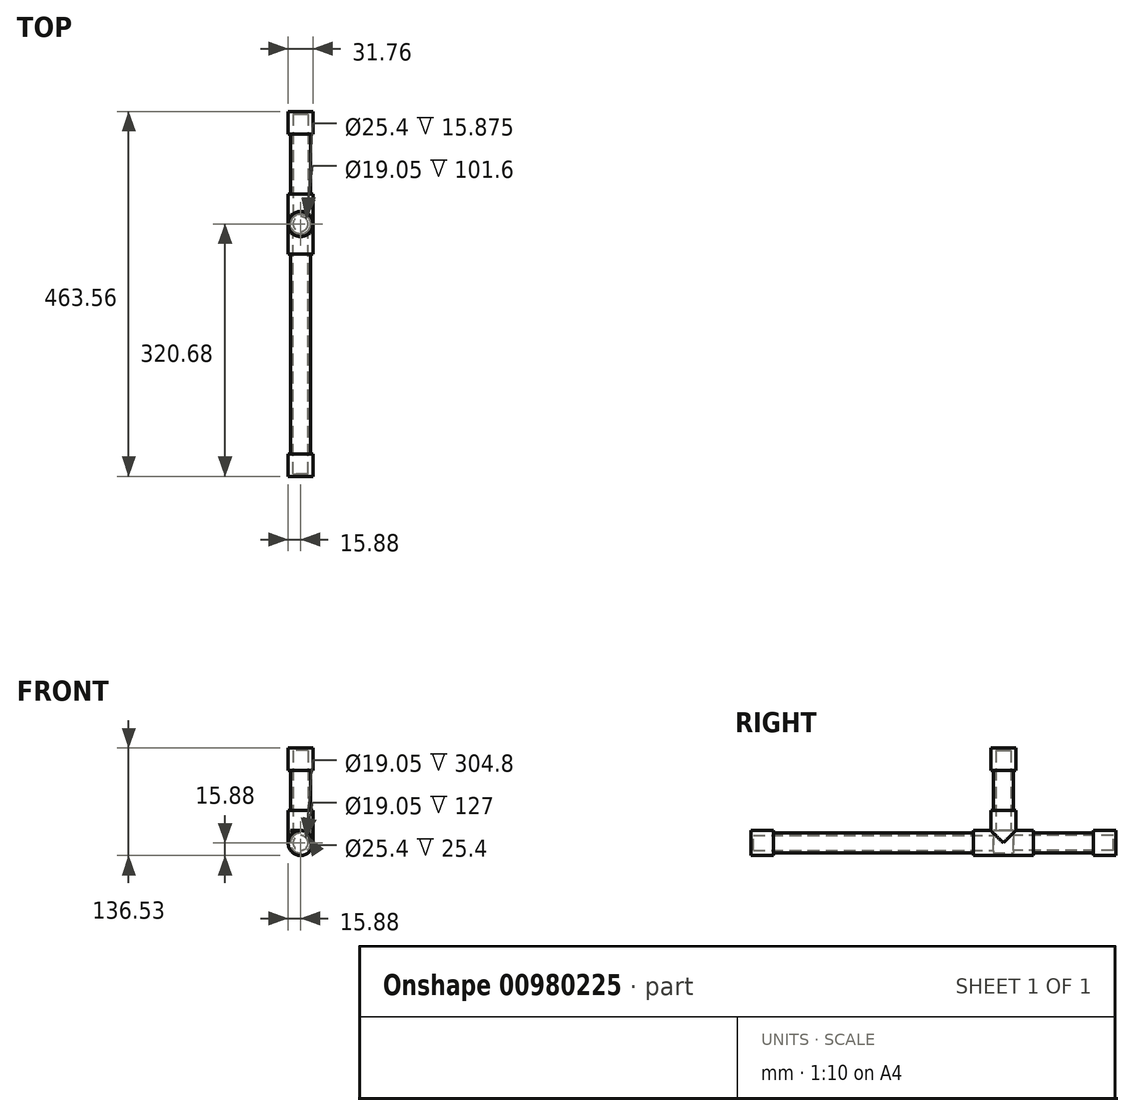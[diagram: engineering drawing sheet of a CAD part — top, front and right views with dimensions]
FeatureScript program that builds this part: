
annotation { "Feature Type Name" : "Feature", "Feature Type Description" : "" }
export const myFeature = defineFeature(function(context is Context, id is Id, definition is map)
    precondition{}
    {
        {
            var Q0;
            Q0=qCreatedBy(makeId("Front.planeOp"),FACE);
            var sketch = newSketch(context, id + "F0", { "sketchPlane" : qUnion([Q0])});
            skCircle(sketch, "E0", {"center": v(0, 0) * mm, "radius": 12.7 * mm});
            skCircle(sketch, "E1", {"center": v(0, 0) * mm, "radius": 9.53 * mm});
            skSolve(sketch);
        }
        {
            var Q0;
            Q0 = qSketchRegion(id + "F0", true);
            extrude(context, id + "F1", {"entities" : qUnion([Q0]), "depth" : 304.8 * mm, "offsetDistance" : 25.4 * mm});
        }
        {
            var Q0;
            Q0=qCreatedBy(makeId("Front.planeOp"),FACE);
            var sketch = newSketch(context, id + "F2", { "sketchPlane" : qUnion([Q0])});
            skCircle(sketch, "E2", {"center": v(0, 0) * mm, "radius": 12.7 * mm});
            skCircle(sketch, "E3", {"center": v(0, 0) * mm, "radius": 15.88 * mm});
            skSolve(sketch);
        }
        {
            var Q0;
            Q0 = qSketchRegion(id + "F2", true);
            extrude(context, id + "F3", {"entities" : qUnion([Q0]), "operationType" : NewBodyOperationType.ADD, "depth" : 25.4 * mm, "offsetDistance" : 25.4 * mm, "hasSecondDirection" : true, "secondDirectionOppositeDirection" : true, "secondDirectionDepth" : 50.8 * mm});
        }
        {
            var Q0;
            Q0=qCreatedBy(makeId("Top.planeOp"),FACE);
            var sketch = newSketch(context, id + "F4", { "sketchPlane" : qUnion([Q0])});
            skCircle(sketch, "E4", {"center": v(0, 12.7) * mm, "radius": 15.88 * mm});
            skCircle(sketch, "E5", {"center": v(0, 12.7) * mm, "radius": 12.7 * mm});
            skSolve(sketch);
        }
        {
            var Q0;
            Q0=makeQuery(id+"F4.imprint","IMPRINT",FACE,{"disambiguationData":[TD([[makeQuery(id+"F4.imprint","IMPRINT",EDGE,{"derivedFrom":sQuery(id+"F4.wireOp",EDGE,"E5")}),1.0]])]});
            extrude(context, id + "F5", {"entities" : qUnion([Q0]), "operationType" : NewBodyOperationType.REMOVE, "depth" : 25.4 * mm, "offsetDistance" : 25.4 * mm});
        }
        {
            var Q0;
            Q0=makeQuery(id+"F4.imprint","IMPRINT",FACE,{"disambiguationData":[TD([[makeQuery(id+"F4.imprint","IMPRINT",EDGE,{"derivedFrom":sQuery(id+"F4.wireOp",EDGE,"E4")}),1.0]])]});
            extrude(context, id + "F6", {"entities" : qUnion([Q0]), "operationType" : NewBodyOperationType.ADD, "depth" : 41.27 * mm, "offsetDistance" : 25.4 * mm});
        }
        {
            var Q0;
            Q0=makeQuery(id+"F2.imprint","IMPRINT",FACE,{"disambiguationData":[TD([[makeQuery(id+"F2.imprint","IMPRINT",EDGE,{"derivedFrom":sQuery(id+"F2.wireOp",EDGE,"E2")}),1.0]])]});
            extrude(context, id + "F7", {"entities" : qUnion([Q0]), "operationType" : NewBodyOperationType.REMOVE, "oppositeDirection" : true, "depth" : 50.8 * mm, "offsetDistance" : 25.4 * mm});
        }
        {
            var Q0;
            Q0=makeQuery(id+"F0.imprint","IMPRINT",FACE,{"disambiguationData":[TD([[makeQuery(id+"F0.imprint","IMPRINT",EDGE,{"derivedFrom":sQuery(id+"F0.wireOp",EDGE,"E1")}),1.0]])]});
            extrude(context, id + "F8", {"entities" : qUnion([Q0]), "operationType" : NewBodyOperationType.REMOVE, "depth" : 25.4 * mm, "offsetDistance" : 25.4 * mm});
        }
        {
            var Q0;
            Q0=makeQuery(id+"F0.imprint","IMPRINT",FACE,{"disambiguationData":[TD([[makeQuery(id+"F0.imprint","IMPRINT",EDGE,{"derivedFrom":sQuery(id+"F0.wireOp",EDGE,"E0")}),1.0]])]});
            extrude(context, id + "F9", {"entities" : qUnion([Q0]), "operationType" : NewBodyOperationType.ADD, "oppositeDirection" : true, "depth" : 152.4 * mm, "offsetDistance" : 25.4 * mm, "hasSecondDirection" : true, "secondDirectionOppositeDirection" : true, "secondDirectionDepth" : 25.4 * mm});
        }
        {
            var Q0;
            Q0=qCreatedBy(makeId("Top.planeOp"),FACE);
            var sketch = newSketch(context, id + "F10", { "sketchPlane" : qUnion([Q0])});
            skCircle(sketch, "E6", {"center": v(0, 12.7) * mm, "radius": 12.7 * mm});
            skCircle(sketch, "E7", {"center": v(0, 12.7) * mm, "radius": 9.53 * mm});
            skSolve(sketch);
        }
        {
            var Q0;
            Q0 = qSketchRegion(id + "F10", true);
            extrude(context, id + "F11", {"entities" : qUnion([Q0]), "operationType" : NewBodyOperationType.ADD, "depth" : 117.47 * mm, "offsetDistance" : 25.4 * mm, "hasSecondDirection" : true, "secondDirectionOppositeDirection" : false, "secondDirectionDepth" : 15.88 * mm});
        }
        {
            var Q0;
            Q0=qCreatedBy(makeId("Right.planeOp"),FACE);
            var sketch = newSketch(context, id + "F12", { "sketchPlane" : qUnion([Q0])});
            skLineSegment(sketch, "E8", {"start": v(152.4, 0) * mm, "end": v(155.58, 0) * mm});
            skLineSegment(sketch, "E9", {"start": v(155.58, 0) * mm, "end": v(155.58, 15.88) * mm});
            skLineSegment(sketch, "E10", {"start": v(155.58, 15.88) * mm, "end": v(127, 15.87) * mm});
            skLineSegment(sketch, "E11", {"start": v(127, 15.87) * mm, "end": v(127, 12.7) * mm});
            skLineSegment(sketch, "E12", {"start": v(127, 12.7) * mm, "end": v(152.4, 12.7) * mm});
            skLineSegment(sketch, "E13", {"start": v(152.4, 12.7) * mm, "end": v(152.4, 0) * mm});
            skLineSegment(sketch, "E14", {"start": v(-304.8, 0) * mm, "end": v(-307.98, 0) * mm});
            skLineSegment(sketch, "E15", {"start": v(-307.98, 0) * mm, "end": v(-307.98, 15.88) * mm});
            skLineSegment(sketch, "E16", {"start": v(-307.98, 15.88) * mm, "end": v(-279.4, 15.88) * mm});
            skLineSegment(sketch, "E17", {"start": v(-279.4, 15.87) * mm, "end": v(-279.4, 12.7) * mm});
            skLineSegment(sketch, "E18", {"start": v(-279.4, 12.7) * mm, "end": v(-304.8, 12.7) * mm});
            skLineSegment(sketch, "E19", {"start": v(-304.8, 12.7) * mm, "end": v(-304.8, 0) * mm});
            skSolve(sketch);
        }
        {
            var Q0;
            Q0 = qSketchRegion(id + "F12", true);
            var Q1;
            Q1=sQuery(id+"F12.wireOp",EDGE,"E14");
            revolve(context, id + "F13", {"operationType" : NewBodyOperationType.ADD, "surfaceOperationType" : NewSurfaceOperationType.NEW, "entities" : qUnion([Q0]), "axis" : qUnion([Q1]), "revolveType" : RevolveType.FULL});
        }
        {
            var Q0;
            Q0=qCreatedBy(makeId("Right.planeOp"),FACE);
            var sketch = newSketch(context, id + "F14", { "sketchPlane" : qUnion([Q0])});
            skLineSegment(sketch, "E20", {"start": v(12.7, 117.48) * mm, "end": v(12.7, 120.65) * mm});
            skLineSegment(sketch, "E21", {"start": v(12.7, 120.65) * mm, "end": v(28.57, 120.65) * mm});
            skLineSegment(sketch, "E22", {"start": v(28.57, 120.65) * mm, "end": v(28.57, 92.08) * mm});
            skLineSegment(sketch, "E23", {"start": v(28.57, 92.08) * mm, "end": v(25.4, 92.08) * mm});
            skLineSegment(sketch, "E24", {"start": v(25.4, 92.08) * mm, "end": v(25.4, 117.48) * mm});
            skLineSegment(sketch, "E25", {"start": v(25.4, 117.48) * mm, "end": v(12.7, 117.48) * mm});
            skSolve(sketch);
        }
        {
            var Q0;
            Q0=makeQuery(id+"F14.imprint","IMPRINT",FACE,{"disambiguationData":[TD([[makeQuery(id+"F14.imprint","IMPRINT",EDGE,{"derivedFrom":sQuery(id+"F14.wireOp",EDGE,"E20")}),-1.0]])]});
            var Q1;
            Q1=sQuery(id+"F14.wireOp",EDGE,"E20");
            revolve(context, id + "F15", {"operationType" : NewBodyOperationType.ADD, "surfaceOperationType" : NewSurfaceOperationType.NEW, "entities" : qUnion([Q0]), "axis" : qUnion([Q1]), "revolveType" : RevolveType.FULL});
        }
    });
